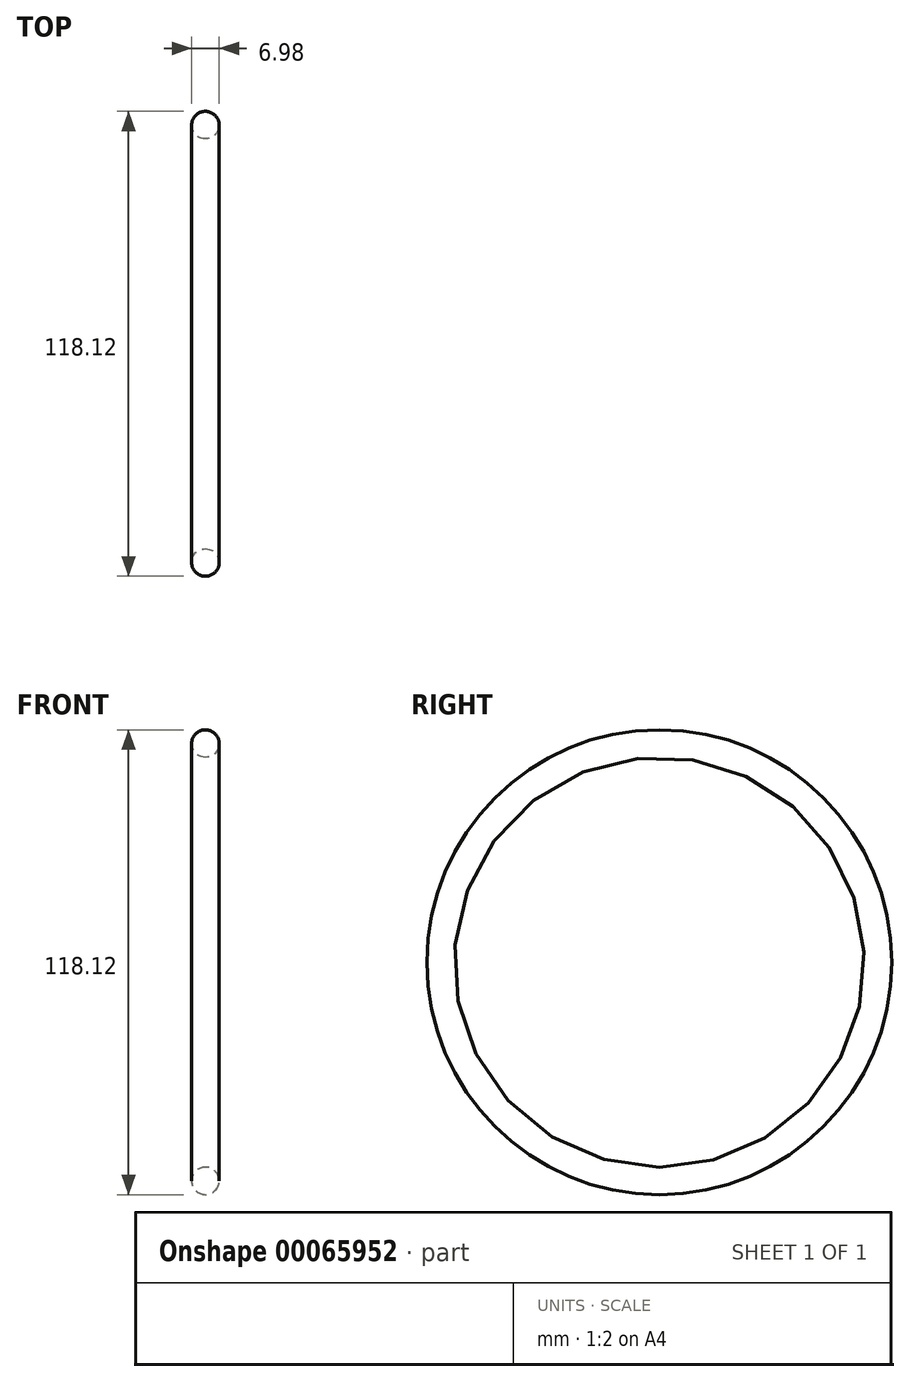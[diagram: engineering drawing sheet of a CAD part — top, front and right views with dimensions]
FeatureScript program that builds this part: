
annotation { "Feature Type Name" : "Feature", "Feature Type Description" : "" }
export const myFeature = defineFeature(function(context is Context, id is Id, definition is map)
    precondition{}
    {
        {
            var Q0;
            Q0=qCreatedBy(makeId("Front.planeOp"),FACE);
            var sketch = newSketch(context, id + "F0", { "sketchPlane" : qUnion([Q0])});
            skLineSegment(sketch, "E0", {"start": v(0, 0) * mm, "end": v(-6.06, 0) * mm, "construction": true});
            skCircle(sketch, "E1", {"center": v(0, 55.56) * mm, "radius": 3.5 * mm});
            skSolve(sketch);
        }
        {
            var Q0;
            Q0=makeQuery(id+"F0.imprint","IMPRINT",FACE,{"disambiguationData":[TD([[makeQuery(id+"F0.imprint","IMPRINT",EDGE,{"derivedFrom":sQuery(id+"F0.wireOp",EDGE,"E1")}),1.0]])]});
            var Q1;
            Q1=sQuery(id+"F0.wireOp",EDGE,"E0");
            revolve(context, id + "F1", {"entities" : qUnion([Q0]), "axis" : qUnion([Q1]), "revolveType" : RevolveType.FULL});
        }
    });
